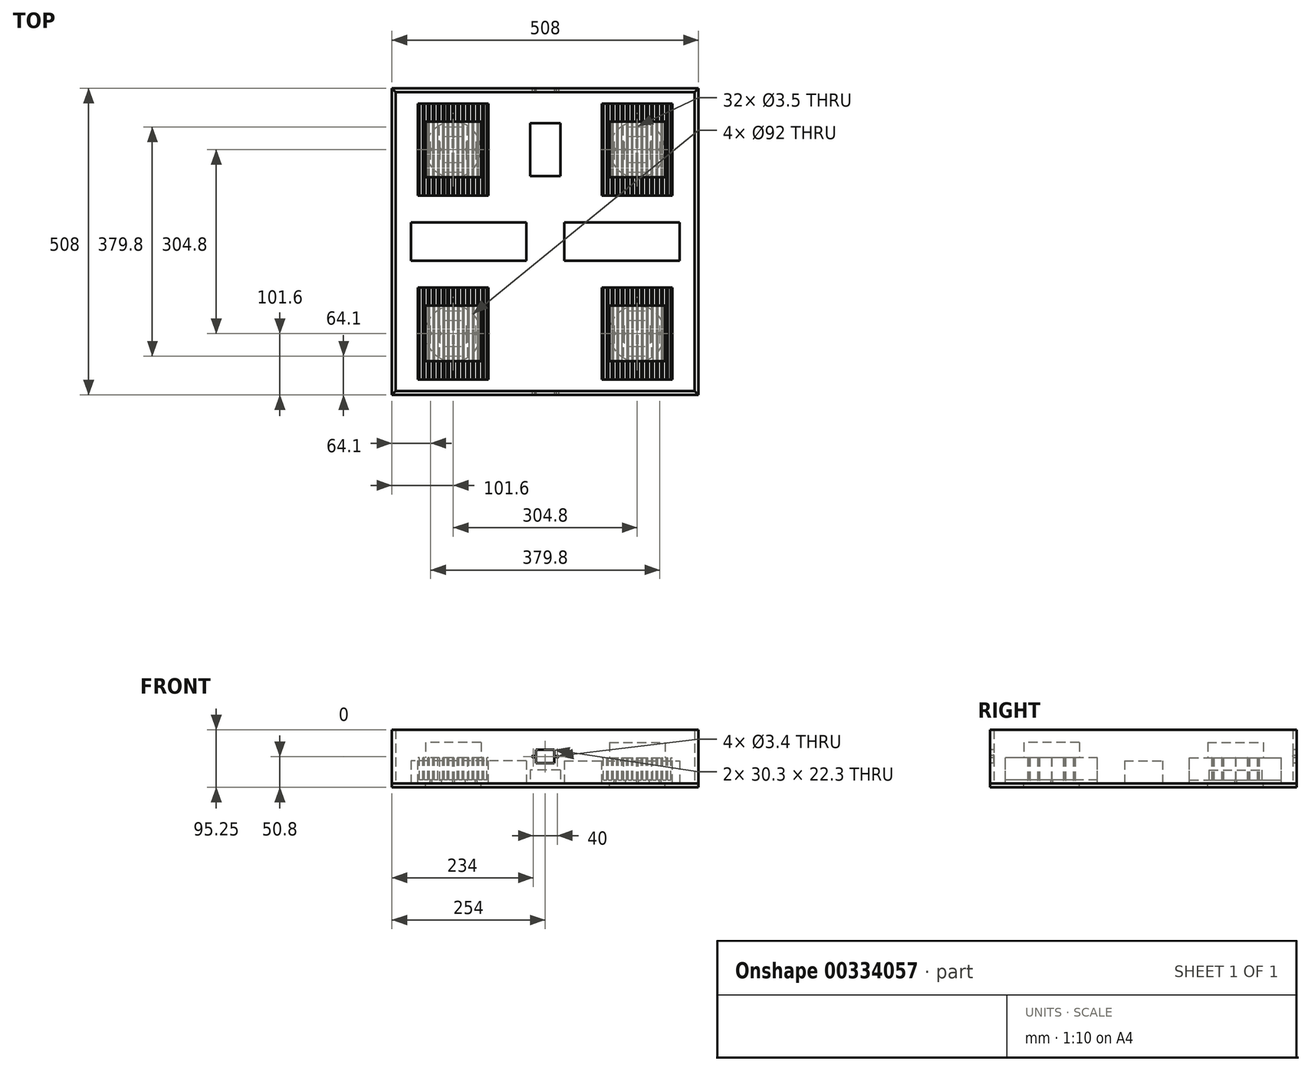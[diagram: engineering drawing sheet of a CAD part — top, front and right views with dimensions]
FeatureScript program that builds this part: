
annotation { "Feature Type Name" : "Feature", "Feature Type Description" : "" }
export const myFeature = defineFeature(function(context is Context, id is Id, definition is map)
    precondition{}
    {
        {
            var Q0;
            Q0=qCreatedBy(makeId("Top.planeOp"),FACE);
            var sketch = newSketch(context, id + "F0", { "sketchPlane" : qUnion([Q0])});
            skLineSegment(sketch, "E0.bottom", {"start": v(304.8, -304.8) * mm, "end": v(-304.8, -304.8) * mm});
            skLineSegment(sketch, "E0.top", {"start": v(304.8, 304.8) * mm, "end": v(-304.8, 304.8) * mm});
            skLineSegment(sketch, "E0.left", {"start": v(304.8, -304.8) * mm, "end": v(304.8, 304.8) * mm});
            skLineSegment(sketch, "E0.right", {"start": v(-304.8, -304.8) * mm, "end": v(-304.8, 304.8) * mm});
            skPoint(sketch, "E0.middle", {"position": v(0, 0) * mm});
            skLineSegment(sketch, "E1", {"start": v(0, 325.47) * mm, "end": v(0, 0) * mm, "construction": true});
            skLineSegment(sketch, "E2", {"start": v(382.98, 0) * mm, "end": v(0, 0) * mm, "construction": true});
            skLineSegment(sketch, "E3.bottom", {"start": v(-93.98, 76.2) * mm, "end": v(-210.82, 76.2) * mm});
            skLineSegment(sketch, "E3.top", {"start": v(-93.98, 228.6) * mm, "end": v(-210.82, 228.6) * mm});
            skLineSegment(sketch, "E3.left", {"start": v(-93.98, 76.2) * mm, "end": v(-93.98, 228.6) * mm});
            skLineSegment(sketch, "E3.right", {"start": v(-210.82, 76.2) * mm, "end": v(-210.82, 228.6) * mm});
            skPoint(sketch, "E3.middle", {"position": v(-152.4, 152.4) * mm});
            skCircle(sketch, "E4", {"center": v(-152.4, 152.4) * mm, "radius": 24.6 * mm});
            skSolve(sketch);
        }
        {
            var Q0;
            Q0=sQuery(id+"F0.wireOp",VERTEX,"E3.top.end");
            var Q1;
            Q1=qCreatedBy(makeId("Front.planeOp"),FACE);
            cPlane(context, id + "F1", {"entities" : qUnion([Q0, Q1]), "cplaneType" : CPlaneType.PLANE_POINT, "offset" : 25.4 * mm, "width" : 152.4 * mm, "height" : 152.4 * mm});
        }
        {
            var Q0;
            Q0=qCreatedBy(id+"F1.planeOp",FACE);
            var sketch = newSketch(context, id + "F2", { "sketchPlane" : qUnion([Q0])});
            skLineSegment(sketch, "E5", {"start": v(-152.4, 0) * mm, "end": v(-152.4, 128.47) * mm, "construction": true});
            skLineSegment(sketch, "E6.bottom", {"start": v(-93.98, 0) * mm, "end": v(-210.82, 0) * mm});
            skLineSegment(sketch, "E6.top", {"start": v(-93.98, 5.84) * mm, "end": v(-210.82, 5.84) * mm});
            skLineSegment(sketch, "E6.left", {"start": v(-93.98, 0) * mm, "end": v(-93.98, 5.84) * mm});
            skLineSegment(sketch, "E6.right", {"start": v(-210.82, 0) * mm, "end": v(-210.82, 5.84) * mm});
            skSolve(sketch);
        }
        {
            var Q0;
            Q0 = qSketchRegion(id + "F2", true);
            var Q1;
            Q1=sQuery(id+"F0.wireOp",VERTEX,"E3.bottom.end");
            extrude(context, id + "F3", {"entities" : qUnion([Q0]), "endBound" : BoundingType.UP_TO_VERTEX, "endBoundEntityVertex" : qUnion([Q1]), "depth" : 25.4 * mm});
        }
        {
            var Q0;
            Q0=makeQuery(id+"F3.opExtrude","CAP_FACE",FACE,{"disambiguationData":[OSD([sQuery(id+"F2.wireOp",EDGE,"E6.bottom"),sQuery(id+"F2.wireOp",EDGE,"E6.top"),sQuery(id+"F2.wireOp",EDGE,"E6.left"),sQuery(id+"F2.wireOp",EDGE,"E6.right")])],"isStart":true});
            var sketch = newSketch(context, id + "F4", { "sketchPlane" : qUnion([Q0])});
            skLineSegment(sketch, "E7.bottom", {"start": v(93.98, 5.84) * mm, "end": v(96.5, 5.84) * mm});
            skLineSegment(sketch, "E7.top", {"start": v(93.98, 42.7) * mm, "end": v(96.5, 42.7) * mm});
            skLineSegment(sketch, "E7.left", {"start": v(93.98, 5.84) * mm, "end": v(93.98, 42.7) * mm});
            skLineSegment(sketch, "E7.right", {"start": v(96.5, 5.84) * mm, "end": v(96.5, 42.7) * mm});
            skLineSegment(sketch, "E8.1.0.0", {"start": v(102.15, 5.84) * mm, "end": v(102.15, 42.7) * mm});
            skLineSegment(sketch, "E8.1.0.1", {"start": v(104.66, 5.84) * mm, "end": v(104.66, 42.7) * mm});
            skLineSegment(sketch, "E8.1.0.2", {"start": v(102.15, 42.7) * mm, "end": v(104.66, 42.7) * mm});
            skLineSegment(sketch, "E8.1.0.3", {"start": v(102.15, 5.84) * mm, "end": v(104.66, 5.84) * mm});
            skLineSegment(sketch, "E8.2.0.0", {"start": v(110.31, 5.84) * mm, "end": v(110.31, 42.7) * mm});
            skLineSegment(sketch, "E8.2.0.1", {"start": v(112.83, 5.84) * mm, "end": v(112.83, 42.7) * mm});
            skLineSegment(sketch, "E8.2.0.2", {"start": v(110.31, 42.7) * mm, "end": v(112.83, 42.7) * mm});
            skLineSegment(sketch, "E8.2.0.3", {"start": v(110.31, 5.84) * mm, "end": v(112.83, 5.84) * mm});
            skLineSegment(sketch, "E8.direction1", {"start": v(93.98, 5.84) * mm, "end": v(102.15, 5.84) * mm, "construction": true});
            skLineSegment(sketch, "E9.0.3.0", {"start": v(118.48, 5.84) * mm, "end": v(118.48, 42.7) * mm});
            skLineSegment(sketch, "E9.3.3.0", {"start": v(121, 5.84) * mm, "end": v(121, 42.7) * mm});
            skLineSegment(sketch, "E9.6.3.0", {"start": v(118.48, 42.7) * mm, "end": v(121, 42.7) * mm});
            skLineSegment(sketch, "E9.9.3.0", {"start": v(118.48, 5.84) * mm, "end": v(121, 5.84) * mm});
            skLineSegment(sketch, "E9.0.4.0", {"start": v(126.64, 5.84) * mm, "end": v(126.64, 42.7) * mm});
            skLineSegment(sketch, "E9.3.4.0", {"start": v(129.16, 5.84) * mm, "end": v(129.16, 42.7) * mm});
            skLineSegment(sketch, "E9.6.4.0", {"start": v(126.64, 42.7) * mm, "end": v(129.16, 42.7) * mm});
            skLineSegment(sketch, "E9.9.4.0", {"start": v(126.64, 5.84) * mm, "end": v(129.16, 5.84) * mm});
            skLineSegment(sketch, "E9.0.5.0", {"start": v(134.81, 5.84) * mm, "end": v(134.81, 42.7) * mm});
            skLineSegment(sketch, "E9.3.5.0", {"start": v(137.33, 5.84) * mm, "end": v(137.33, 42.7) * mm});
            skLineSegment(sketch, "E9.6.5.0", {"start": v(134.81, 42.7) * mm, "end": v(137.33, 42.7) * mm});
            skLineSegment(sketch, "E9.9.5.0", {"start": v(134.81, 5.84) * mm, "end": v(137.33, 5.84) * mm});
            skLineSegment(sketch, "E9.0.6.0", {"start": v(142.98, 5.84) * mm, "end": v(142.98, 42.7) * mm});
            skLineSegment(sketch, "E9.3.6.0", {"start": v(145.5, 5.84) * mm, "end": v(145.5, 42.7) * mm});
            skLineSegment(sketch, "E9.6.6.0", {"start": v(142.98, 42.7) * mm, "end": v(145.5, 42.7) * mm});
            skLineSegment(sketch, "E9.9.6.0", {"start": v(142.98, 5.84) * mm, "end": v(145.5, 5.84) * mm});
            skLineSegment(sketch, "E9.0.7.0", {"start": v(151.14, 5.84) * mm, "end": v(151.14, 42.7) * mm});
            skLineSegment(sketch, "E9.3.7.0", {"start": v(153.66, 5.84) * mm, "end": v(153.66, 42.7) * mm});
            skLineSegment(sketch, "E9.6.7.0", {"start": v(151.14, 42.7) * mm, "end": v(153.66, 42.7) * mm});
            skLineSegment(sketch, "E9.9.7.0", {"start": v(151.14, 5.84) * mm, "end": v(153.66, 5.84) * mm});
            skLineSegment(sketch, "E9.0.8.0", {"start": v(159.3, 5.84) * mm, "end": v(159.3, 42.7) * mm});
            skLineSegment(sketch, "E9.3.8.0", {"start": v(161.82, 5.84) * mm, "end": v(161.82, 42.7) * mm});
            skLineSegment(sketch, "E9.6.8.0", {"start": v(159.3, 42.7) * mm, "end": v(161.82, 42.7) * mm});
            skLineSegment(sketch, "E9.9.8.0", {"start": v(159.3, 5.84) * mm, "end": v(161.82, 5.84) * mm});
            skLineSegment(sketch, "E9.0.9.0", {"start": v(167.47, 5.84) * mm, "end": v(167.47, 42.7) * mm});
            skLineSegment(sketch, "E9.3.9.0", {"start": v(169.99, 5.84) * mm, "end": v(169.99, 42.7) * mm});
            skLineSegment(sketch, "E9.6.9.0", {"start": v(167.47, 42.7) * mm, "end": v(169.99, 42.7) * mm});
            skLineSegment(sketch, "E9.9.9.0", {"start": v(167.47, 5.84) * mm, "end": v(169.99, 5.84) * mm});
            skLineSegment(sketch, "E9.0.10.0", {"start": v(175.64, 5.84) * mm, "end": v(175.64, 42.7) * mm});
            skLineSegment(sketch, "E9.3.10.0", {"start": v(178.16, 5.84) * mm, "end": v(178.16, 42.7) * mm});
            skLineSegment(sketch, "E9.6.10.0", {"start": v(175.64, 42.7) * mm, "end": v(178.16, 42.7) * mm});
            skLineSegment(sketch, "E9.9.10.0", {"start": v(175.64, 5.84) * mm, "end": v(178.16, 5.84) * mm});
            skLineSegment(sketch, "E9.0.11.0", {"start": v(183.8, 5.84) * mm, "end": v(183.8, 42.7) * mm});
            skLineSegment(sketch, "E9.3.11.0", {"start": v(186.32, 5.84) * mm, "end": v(186.32, 42.7) * mm});
            skLineSegment(sketch, "E9.6.11.0", {"start": v(183.8, 42.7) * mm, "end": v(186.32, 42.7) * mm});
            skLineSegment(sketch, "E9.9.11.0", {"start": v(183.8, 5.84) * mm, "end": v(186.32, 5.84) * mm});
            skLineSegment(sketch, "E9.0.12.0", {"start": v(191.97, 5.84) * mm, "end": v(191.97, 42.7) * mm});
            skLineSegment(sketch, "E9.3.12.0", {"start": v(194.49, 5.84) * mm, "end": v(194.49, 42.7) * mm});
            skLineSegment(sketch, "E9.6.12.0", {"start": v(191.97, 42.7) * mm, "end": v(194.49, 42.7) * mm});
            skLineSegment(sketch, "E9.9.12.0", {"start": v(191.97, 5.84) * mm, "end": v(194.49, 5.84) * mm});
            skLineSegment(sketch, "E9.0.13.0", {"start": v(200.14, 5.84) * mm, "end": v(200.14, 42.7) * mm});
            skLineSegment(sketch, "E9.3.13.0", {"start": v(202.65, 5.84) * mm, "end": v(202.65, 42.7) * mm});
            skLineSegment(sketch, "E9.6.13.0", {"start": v(200.14, 42.7) * mm, "end": v(202.65, 42.7) * mm});
            skLineSegment(sketch, "E9.9.13.0", {"start": v(200.14, 5.84) * mm, "end": v(202.65, 5.84) * mm});
            skLineSegment(sketch, "E9.0.14.0", {"start": v(208.3, 5.84) * mm, "end": v(208.3, 42.7) * mm});
            skLineSegment(sketch, "E9.3.14.0", {"start": v(210.82, 5.84) * mm, "end": v(210.82, 42.7) * mm});
            skLineSegment(sketch, "E9.6.14.0", {"start": v(208.3, 42.7) * mm, "end": v(210.82, 42.7) * mm});
            skLineSegment(sketch, "E9.9.14.0", {"start": v(208.3, 5.84) * mm, "end": v(210.82, 5.84) * mm});
            skSolve(sketch);
        }
        {
            var Q0;
            Q0 = qSketchRegion(id + "F4", true);
            var Q1;
            Q1=makeQuery(id+"F3.opExtrude","CAP_FACE",FACE,{"disambiguationData":[OSD([sQuery(id+"F2.wireOp",EDGE,"E6.bottom"),sQuery(id+"F2.wireOp",EDGE,"E6.top"),sQuery(id+"F2.wireOp",EDGE,"E6.left"),sQuery(id+"F2.wireOp",EDGE,"E6.right")])],"isStart":false});
            extrude(context, id + "F5", {"entities" : qUnion([Q0]), "operationType" : NewBodyOperationType.ADD, "endBound" : BoundingType.UP_TO_SURFACE, "oppositeDirection" : true, "endBoundEntityFace" : qUnion([Q1]), "depth" : 25.4 * mm});
        }
        {
            var Q0;
            Q0=makeQuery(id+"F0.imprint","IMPRINT",FACE,{"disambiguationData":[TD([[makeQuery(id+"F0.imprint","IMPRINT",EDGE,{"derivedFrom":sQuery(id+"F0.wireOp",EDGE,"E3.bottom")}),-1.0]])]});
            var sketch = newSketch(context, id + "F6", { "sketchPlane" : qUnion([Q0])});
            skCircle(sketch, "E10", {"center": v(-173.9, 152.4) * mm, "radius": 1.75 * mm});
            skLineSegment(sketch, "E11", {"start": v(-152.4, 111.93) * mm, "end": v(-152.4, 152.4) * mm, "construction": true});
            skCircle(sketch, "E12.1.0", {"center": v(-152.4, 130.9) * mm, "radius": 1.75 * mm});
            skCircle(sketch, "E12.2.0", {"center": v(-130.9, 152.4) * mm, "radius": 1.75 * mm});
            skCircle(sketch, "E12.3.0", {"center": v(-152.4, 173.9) * mm, "radius": 1.75 * mm});
            skPoint(sketch, "E12.center", {"position": v(-152.4, 152.4) * mm});
            skCircle(sketch, "E13", {"center": v(-189.9, 152.4) * mm, "radius": 1.75 * mm});
            skCircle(sketch, "E14.1.0", {"center": v(-152.4, 114.9) * mm, "radius": 1.75 * mm});
            skCircle(sketch, "E14.2.0", {"center": v(-114.9, 152.4) * mm, "radius": 1.75 * mm});
            skCircle(sketch, "E14.3.0", {"center": v(-152.4, 189.9) * mm, "radius": 1.75 * mm});
            skSolve(sketch);
        }
        {
            var Q0;
            Q0 = qSketchRegion(id + "F6", true);
            extrude(context, id + "F7", {"entities" : qUnion([Q0]), "operationType" : NewBodyOperationType.REMOVE, "endBound" : BoundingType.THROUGH_ALL, "depth" : 25.4 * mm});
        }
        {
            var Q0;
            Q0=makeQuery(id+"F3.opExtrude","SWEPT_BODY",BODY,{"disambiguationData":[OSD([sQuery(id+"F2.wireOp",EDGE,"E6.bottom"),sQuery(id+"F2.wireOp",EDGE,"E6.top"),sQuery(id+"F2.wireOp",EDGE,"E6.left"),sQuery(id+"F2.wireOp",EDGE,"E6.right")])]});
            var Q1;
            Q1=qCreatedBy(makeId("Right.planeOp"),FACE);
            mirror(context, id + "F8", {"entities" : qUnion([Q0]), "mirrorPlane" : qUnion([Q1])});
        }
        {
            var Q0;
            Q0=makeQuery(id+"F3.opExtrude","SWEPT_BODY",BODY,{"disambiguationData":[OSD([sQuery(id+"F2.wireOp",EDGE,"E6.bottom"),sQuery(id+"F2.wireOp",EDGE,"E6.top"),sQuery(id+"F2.wireOp",EDGE,"E6.left"),sQuery(id+"F2.wireOp",EDGE,"E6.right")])]});
            var Q1;
            Q1=makeQuery(id+"F8.opPattern","COPY",BODY,{"derivedFrom":makeQuery(id+"F3.opExtrude","SWEPT_BODY",BODY,{"disambiguationData":[OSD([sQuery(id+"F2.wireOp",EDGE,"E6.bottom"),sQuery(id+"F2.wireOp",EDGE,"E6.top"),sQuery(id+"F2.wireOp",EDGE,"E6.left"),sQuery(id+"F2.wireOp",EDGE,"E6.right")])]}),"instanceName":"1"});
            var Q2;
            Q2=qCreatedBy(makeId("Front.planeOp"),FACE);
            mirror(context, id + "F9", {"entities" : qUnion([Q0, Q1]), "mirrorPlane" : qUnion([Q2])});
        }
        {
            var Q0;
            Q0=makeQuery(id+"F9.opPattern","COPY",FACE,{"derivedFrom":makeQuery(id+"F3.opExtrude","SWEPT_FACE",FACE,{"disambiguationData":[OSD([sQuery(id+"F2.wireOp",EDGE,"E6.bottom")])]}),"instanceName":"1"});
            var sketch = newSketch(context, id + "F10", { "sketchPlane" : qUnion([Q0])});
            skLineSegment(sketch, "E15.bottom", {"start": v(254, -254) * mm, "end": v(-254, -254) * mm});
            skLineSegment(sketch, "E15.top", {"start": v(254, 254) * mm, "end": v(-254, 254) * mm});
            skLineSegment(sketch, "E15.left", {"start": v(254, -254) * mm, "end": v(254, 254) * mm});
            skLineSegment(sketch, "E15.right", {"start": v(-254, -254) * mm, "end": v(-254, 254) * mm});
            skPoint(sketch, "E15.middle", {"position": v(0, 0) * mm});
            skCircle(sketch, "E16", {"center": v(-152.4, -152.4) * mm, "radius": 46 * mm});
            skLineSegment(sketch, "E17.0", {"start": v(0, -325.47) * mm, "end": v(0, 0) * mm, "construction": true});
            skLineSegment(sketch, "E18.0", {"start": v(382.98, 0) * mm, "end": v(0, 0) * mm, "construction": true});
            skCircle(sketch, "E19.MirrorC", {"center": v(152.4, -152.4) * mm, "radius": 46 * mm});
            skCircle(sketch, "E20.MirrorC", {"center": v(-152.4, 152.4) * mm, "radius": 46 * mm});
            skCircle(sketch, "E21.MirrorC", {"center": v(152.4, 152.4) * mm, "radius": 46 * mm});
            skSolve(sketch);
        }
        {
            var Q0;
            Q0 = qSketchRegion(id + "F10", true);
            extrude(context, id + "F11", {"entities" : qUnion([Q0]), "depth" : 6.35 * mm});
        }
        {
            var Q0;
            Q0=makeQuery(id+"F9.opPattern","COPY",FACE,{"derivedFrom":makeQuery(id+"F7.boolean.opBoolean","SPLIT",FACE,{"disambiguationData":[TD([makeQuery(id+"F5.opExtrude","SWEPT_FACE",FACE,{"disambiguationData":[OSD([sQuery(id+"F4.wireOp",EDGE,"E9.0.7.0")])]}),makeQuery(id+"F5.opExtrude","SWEPT_FACE",FACE,{"disambiguationData":[OSD([sQuery(id+"F4.wireOp",EDGE,"E9.3.7.0")])]}),makeQuery(id+"F7.opExtrude","SWEPT_FACE",FACE,{"disambiguationData":[OSD([sQuery(id+"F6.wireOp",EDGE,"E12.1.0")])]}),makeQuery(id+"F7.opExtrude","SWEPT_FACE",FACE,{"disambiguationData":[OSD([sQuery(id+"F6.wireOp",EDGE,"E12.3.0")])]})])],"derivedFrom":makeQuery(id+"F5.opExtrude","SWEPT_FACE",FACE,{"disambiguationData":[OSD([sQuery(id+"F4.wireOp",EDGE,"E9.6.7.0")])]})}),"instanceName":"1"});
            var sketch = newSketch(context, id + "F12", { "sketchPlane" : qUnion([Q0])});
            skLineSegment(sketch, "E22.bottom", {"start": v(-106.4, 106.4) * mm, "end": v(-198.4, 106.4) * mm});
            skLineSegment(sketch, "E22.top", {"start": v(-106.4, 198.4) * mm, "end": v(-198.4, 198.4) * mm});
            skLineSegment(sketch, "E22.left", {"start": v(-106.4, 106.4) * mm, "end": v(-106.4, 198.4) * mm});
            skLineSegment(sketch, "E22.right", {"start": v(-198.4, 106.4) * mm, "end": v(-198.4, 198.4) * mm});
            skPoint(sketch, "E22.middle", {"position": v(-152.4, 152.4) * mm});
            skPoint(sketch, "E23", {"position": v(-151.14, -152.4) * mm});
            skLineSegment(sketch, "E24.0", {"start": v(0, 325.47) * mm, "end": v(0, 0) * mm, "construction": true});
            skLineSegment(sketch, "E25.0", {"start": v(382.98, 0) * mm, "end": v(0, 0) * mm, "construction": true});
            skLineSegment(sketch, "E26.MirrorCS", {"start": v(198.4, 106.4) * mm, "end": v(198.4, 198.4) * mm});
            skLineSegment(sketch, "E27.MirrorCS", {"start": v(106.4, 106.4) * mm, "end": v(198.4, 106.4) * mm});
            skLineSegment(sketch, "E28.MirrorCS", {"start": v(106.4, 106.4) * mm, "end": v(106.4, 198.4) * mm});
            skLineSegment(sketch, "E29.MirrorCS", {"start": v(106.4, 198.4) * mm, "end": v(198.4, 198.4) * mm});
            skPoint(sketch, "E30.MirrorP", {"position": v(152.4, 152.4) * mm});
            skLineSegment(sketch, "E31.MirrorCS", {"start": v(106.4, -198.4) * mm, "end": v(198.4, -198.4) * mm});
            skLineSegment(sketch, "E32.MirrorCS", {"start": v(-106.4, -106.4) * mm, "end": v(-106.4, -198.4) * mm});
            skLineSegment(sketch, "E33.MirrorCS", {"start": v(-106.4, -198.4) * mm, "end": v(-198.4, -198.4) * mm});
            skLineSegment(sketch, "E34.MirrorCS", {"start": v(-106.4, -106.4) * mm, "end": v(-198.4, -106.4) * mm});
            skLineSegment(sketch, "E35.MirrorCS", {"start": v(198.4, -106.4) * mm, "end": v(198.4, -198.4) * mm});
            skPoint(sketch, "E36.MirrorP", {"position": v(152.4, -152.4) * mm});
            skLineSegment(sketch, "E37.MirrorCS", {"start": v(-198.4, -106.4) * mm, "end": v(-198.4, -198.4) * mm});
            skPoint(sketch, "E38.MirrorP", {"position": v(-152.4, -152.4) * mm});
            skLineSegment(sketch, "E39.MirrorCS", {"start": v(106.4, -106.4) * mm, "end": v(106.4, -198.4) * mm});
            skLineSegment(sketch, "E40.MirrorCS", {"start": v(106.4, -106.4) * mm, "end": v(198.4, -106.4) * mm});
            skSolve(sketch);
        }
        {
            var Q0;
            Q0 = qSketchRegion(id + "F12", true);
            extrude(context, id + "F13", {"entities" : qUnion([Q0]), "depth" : 25 * mm});
        }
        {
            var Q0;
            Q0=makeQuery(id+"F0.imprint","IMPRINT",FACE,{"disambiguationData":[TD([[makeQuery(id+"F0.imprint","IMPRINT",EDGE,{"derivedFrom":sQuery(id+"F0.wireOp",EDGE,"E0.bottom")}),-1.0]])]});
            var sketch = newSketch(context, id + "F14", { "sketchPlane" : qUnion([Q0])});
            skLineSegment(sketch, "E41", {"start": v(-254, 254) * mm, "end": v(-254, -254) * mm});
            skLineSegment(sketch, "E42", {"start": v(-254, -254) * mm, "end": v(-247.65, -247.65) * mm});
            skLineSegment(sketch, "E43", {"start": v(-247.65, -247.65) * mm, "end": v(-247.65, 247.65) * mm});
            skLineSegment(sketch, "E44", {"start": v(-247.65, 247.65) * mm, "end": v(-254, 254) * mm});
            skSolve(sketch);
        }
        {
            var Q0;
            Q0 = qSketchRegion(id + "F14", true);
            extrude(context, id + "F15", {"entities" : qUnion([Q0]), "depth" : 88.9 * mm});
        }
        {
            var Q0;
            Q0=qCreatedBy(makeId("Front.planeOp"),FACE);
            var sketch = newSketch(context, id + "F16", { "sketchPlane" : qUnion([Q0])});
            skLineSegment(sketch, "E45", {"start": v(0, 0) * mm, "end": v(0, 322.81) * mm, "construction": true});
            skSolve(sketch);
        }
        {
            var Q0;
            Q0=makeQuery(id+"F15.opExtrude","SWEPT_BODY",BODY,{"disambiguationData":[OSD([sQuery(id+"F14.wireOp",EDGE,"E41"),sQuery(id+"F14.wireOp",EDGE,"E42"),sQuery(id+"F14.wireOp",EDGE,"E43"),sQuery(id+"F14.wireOp",EDGE,"E44")])]});
            var Q1;
            Q1=sQuery(id+"F16.wireOp",EDGE,"E45");
            circularPattern(context, id + "F17", {"entities" : qUnion([Q0]), "axis" : qUnion([Q1]), "angle" : 360 * degree, "instanceCount" : 4, "equalSpace" : true});
        }
        {
            var Q0;
            Q0=makeQuery(id+"F17.opPattern","COPY",FACE,{"derivedFrom":makeQuery(id+"F15.opExtrude","SWEPT_FACE",FACE,{"disambiguationData":[OSD([sQuery(id+"F14.wireOp",EDGE,"E41")])]}),"instanceName":"1"});
            var sketch = newSketch(context, id + "F18", { "sketchPlane" : qUnion([Q0])});
            skLineSegment(sketch, "E46", {"start": v(0, 0) * mm, "end": v(0, 88.9) * mm, "construction": true});
            skLineSegment(sketch, "E47", {"start": v(-254, 44.45) * mm, "end": v(0, 44.45) * mm, "construction": true});
            skLineSegment(sketch, "E48.bottom", {"start": v(15.15, 33.3) * mm, "end": v(-15.15, 33.3) * mm});
            skLineSegment(sketch, "E48.top", {"start": v(15.15, 55.6) * mm, "end": v(-15.15, 55.6) * mm});
            skLineSegment(sketch, "E48.left", {"start": v(15.15, 33.3) * mm, "end": v(15.15, 55.6) * mm});
            skLineSegment(sketch, "E48.right", {"start": v(-15.15, 33.3) * mm, "end": v(-15.15, 55.6) * mm});
            skPoint(sketch, "E48.middle", {"position": v(0, 44.45) * mm});
            skCircle(sketch, "E49", {"center": v(-20, 44.45) * mm, "radius": 1.7 * mm});
            skCircle(sketch, "E50.MirrorC", {"center": v(20, 44.45) * mm, "radius": 1.7 * mm});
            skSolve(sketch);
        }
        {
            var Q0;
            Q0 = qSketchRegion(id + "F18", true);
            extrude(context, id + "F19", {"entities" : qUnion([Q0]), "operationType" : NewBodyOperationType.REMOVE, "endBound" : BoundingType.THROUGH_ALL, "oppositeDirection" : true, "depth" : 25.4 * mm});
        }
        {
            var Q0;
            Q0=makeQuery(id+"F11.opExtrude","CAP_FACE",FACE,{"disambiguationData":[OSD([sQuery(id+"F10.wireOp",EDGE,"E15.bottom"),sQuery(id+"F10.wireOp",EDGE,"E15.top"),sQuery(id+"F10.wireOp",EDGE,"E15.left"),sQuery(id+"F10.wireOp",EDGE,"E15.right"),sQuery(id+"F10.wireOp",EDGE,"E16"),sQuery(id+"F10.wireOp",EDGE,"E19.MirrorC"),sQuery(id+"F10.wireOp",EDGE,"E20.MirrorC"),sQuery(id+"F10.wireOp",EDGE,"E21.MirrorC")])],"isStart":true});
            var sketch = newSketch(context, id + "F20", { "sketchPlane" : qUnion([Q0])});
            skLineSegment(sketch, "E51.bottom", {"start": v(-31.5, -31.5) * mm, "end": v(-222.5, -31.5) * mm});
            skLineSegment(sketch, "E51.top", {"start": v(-31.5, 31.5) * mm, "end": v(-222.5, 31.5) * mm});
            skLineSegment(sketch, "E51.left", {"start": v(-31.5, -31.5) * mm, "end": v(-31.5, 31.5) * mm});
            skLineSegment(sketch, "E51.right", {"start": v(-222.5, -31.5) * mm, "end": v(-222.5, 31.5) * mm});
            skPoint(sketch, "E51.middle", {"position": v(-127, 0) * mm});
            skLineSegment(sketch, "E52", {"start": v(0, 0) * mm, "end": v(0, 175.51) * mm, "construction": true});
            skLineSegment(sketch, "E53.MirrorCS", {"start": v(222.5, -31.5) * mm, "end": v(222.5, 31.5) * mm});
            skPoint(sketch, "E54.MirrorP", {"position": v(127, 0) * mm});
            skLineSegment(sketch, "E55.MirrorCS", {"start": v(31.5, 31.5) * mm, "end": v(222.5, 31.5) * mm});
            skLineSegment(sketch, "E56.MirrorCS", {"start": v(31.5, -31.5) * mm, "end": v(31.5, 31.5) * mm});
            skLineSegment(sketch, "E57.MirrorCS", {"start": v(31.5, -31.5) * mm, "end": v(222.5, -31.5) * mm});
            skSolve(sketch);
        }
        {
            var Q0;
            Q0 = qSketchRegion(id + "F20", true);
            extrude(context, id + "F21", {"entities" : qUnion([Q0]), "depth" : 37.5 * mm});
        }
        {
            var Q0;
            Q0=makeQuery(id+"F11.opExtrude","CAP_FACE",FACE,{"disambiguationData":[OSD([sQuery(id+"F10.wireOp",EDGE,"E15.bottom"),sQuery(id+"F10.wireOp",EDGE,"E15.top"),sQuery(id+"F10.wireOp",EDGE,"E15.left"),sQuery(id+"F10.wireOp",EDGE,"E15.right"),sQuery(id+"F10.wireOp",EDGE,"E16"),sQuery(id+"F10.wireOp",EDGE,"E19.MirrorC"),sQuery(id+"F10.wireOp",EDGE,"E20.MirrorC"),sQuery(id+"F10.wireOp",EDGE,"E21.MirrorC")])],"isStart":true});
            var sketch = newSketch(context, id + "F22", { "sketchPlane" : qUnion([Q0])});
            skLineSegment(sketch, "E58.bottom", {"start": v(25, 108.65) * mm, "end": v(-25, 108.65) * mm});
            skLineSegment(sketch, "E58.top", {"start": v(25, 196.15) * mm, "end": v(-25, 196.15) * mm});
            skLineSegment(sketch, "E58.left", {"start": v(25, 108.65) * mm, "end": v(25, 196.15) * mm});
            skLineSegment(sketch, "E58.right", {"start": v(-25, 108.65) * mm, "end": v(-25, 196.15) * mm});
            skPoint(sketch, "E58.middle", {"position": v(0, 152.4) * mm});
            skSolve(sketch);
        }
        {
            var Q0;
            Q0 = qSketchRegion(id + "F22", true);
            extrude(context, id + "F23", {"entities" : qUnion([Q0]), "depth" : 22 * mm});
        }
    });
